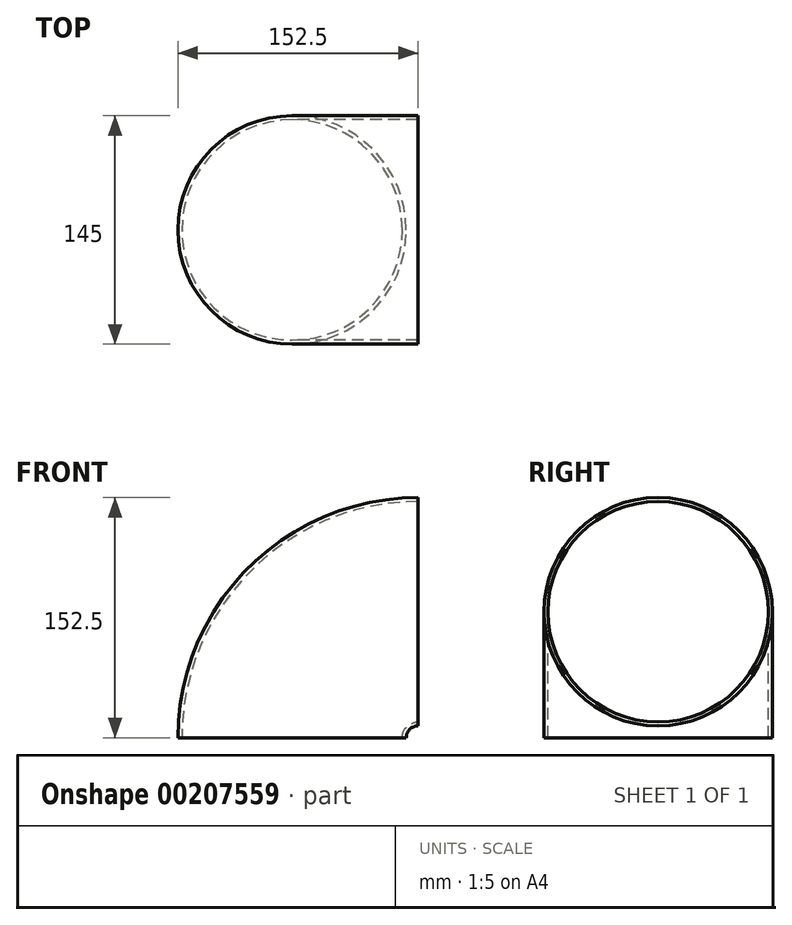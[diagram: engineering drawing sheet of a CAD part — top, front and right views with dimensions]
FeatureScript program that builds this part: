
annotation { "Feature Type Name" : "Feature", "Feature Type Description" : "" }
export const myFeature = defineFeature(function(context is Context, id is Id, definition is map)
    precondition{}
    {
        {
            var Q0;
            Q0=qCreatedBy(makeId("Front.planeOp"),FACE);
            var sketch = newSketch(context, id + "F0", { "sketchPlane" : qUnion([Q0])});
            skArc(sketch, "E0", {"start": v(0, 80) * mm, "mid": v(-56.57, 56.57) * mm, "end": v(-80, 0) * mm});
            skLineSegment(sketch, "E1", {"start": v(0, 0) * mm, "end": v(0, 80) * mm, "construction": true});
            skLineSegment(sketch, "E2", {"start": v(0, 0) * mm, "end": v(-80, 0) * mm, "construction": true});
            skSolve(sketch);
        }
        {
            var Q0;
            Q0=qCreatedBy(makeId("Top.planeOp"),FACE);
            var sketch = newSketch(context, id + "F1", { "sketchPlane" : qUnion([Q0])});
            skCircle(sketch, "E3", {"center": v(-80, 0) * mm, "radius": 70 * mm});
            skCircle(sketch, "E4", {"center": v(-80, 0) * mm, "radius": 72.5 * mm});
            skSolve(sketch);
        }
        {
            var Q0;
            Q0 = qSketchRegion(id + "F1", true);
            var Q1;
            Q1 = qConstructionFilter(qBodyType(qCreatedBy(id + "F0" ,EDGE), BodyType.WIRE), ConstructionObject.NO);
            sweep(context, id + "F2", {"profiles" : qUnion([Q0]), "path" : qUnion([Q1])});
        }
    });
